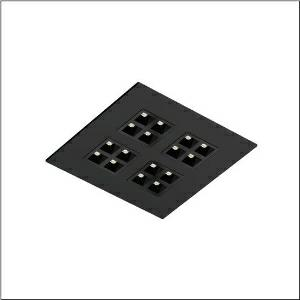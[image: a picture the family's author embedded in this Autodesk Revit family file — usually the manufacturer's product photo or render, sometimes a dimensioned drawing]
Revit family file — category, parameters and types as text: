
# Revit family: silica_31_square_51my6ldu34ba
name_source: partatom
category: Lighting Fixtures
units: mm (PartAtom-declared; Revit-internal decimal feet)

## family parameters
Cut with Voids When Loaded = No
Host = Face
Light Source = No
Part Type = Normal
Room Calculation Point = No
Round Connector Dimension = Use Diameter
Shared = No

## types (1)
- --- (1 x LED, 5980 lm, 38.5 W, 3000K)
    Apparent Load = 39 VA
    CIE Flux Codes = 82 100 100 100 100
    Color Rendering = 80
    Color Temperature = 3000K
    Default Elevation = 1800 mm
    Description = Silica 31 Square, office luminaire, primary light control with lens, of PMMA, primary anti-glare with reflector, of PC, black, light emission: direct distribution, primary light characteristic: symmetric, installation type: lay-in mounting, LED, rated luminous flux: 4.650lm, luminous efficacy: 158lm/W, light colour: 830, colour temperature: 3000K, control gear: DALI 2, Multilumen, with terminal, 5-pole, mains connection: 220..240V, AC, 50/60Hz, rated input power: 29.4W, luminaire housing, of sheet steel, coated, jet black (RAL 9005), module: M625, length: 620mm, width: 620mm, height: 43mm, protection rating (complete): IP20, insulation class (complete): insulation class II (safety insulation), certification: CE, impact resistance: IK03, permissible operating ambient temperature: -20..+35°C, standard: EN 50419, packaging unit: 1 piece
    Height = 0 mm  [stored 0 ft]
    Lamp = 1 x LED
    Lamp Light Flux = 5980 lm
    Lamp Power = 38.5 W
    Lamp count = 1
    Length = 620 mm
    Luminous efficacy = 155 lm/W
    Manufacturer = Siteco
    ModVariant = No
    Model = 51MY6LDU34BA
    Mounting Place = Ceiling
    Mounting Type = Recessed
    Number of Poles = 1
    OnlyDefault = Yes
    Power Factor = 1
    Product Name = Silica 31 Square
    Product group = office luminaire | ceiling recessed
    ProductGroupID = 400
    Protection Class = Protection class II
    Protection Degree = IP 20
    RLX_Detail_Level = 1
    RLX_Emergency_Light_Flux = 0 lm
    RLX_Emergency_Type = 0
    RLX_Emergency_Type_DB = No
    RlxData = <blob elided: 35525 chars, md5=f8309df3>
    Socket = socket
    Standby Power = 0 W
    System Light Flux = 5980 lm
    System Power = 39 W
    Type Comments = factory setting: luminous flux: 100 % | (OFF | OFF | OFF | OFF) | 1050 mA
    Type Image = l_1313660.jpg
    URL = http://relux.com
    VarID = @adj_043275
    Voltage = 0 V
    Weight = 0.00 kg
    Width = 620 mm

note: [stored X ft] marks values corroborated as IEEE doubles in the binary element streams (Revit-internal decimal feet)

## geometry (parser evidence)
native form markers: Blend x4, Sweep x11
no freeform markers — native parametric forms only
